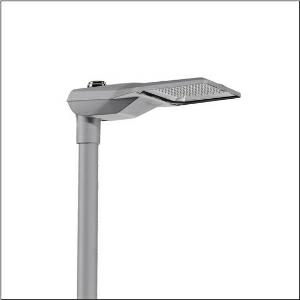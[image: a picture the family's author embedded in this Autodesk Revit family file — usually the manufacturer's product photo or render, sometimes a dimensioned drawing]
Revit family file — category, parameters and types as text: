
# Revit family: streetlight_sl_21_midi___st1_0a_5xe7d27n08nb_1197
name_source: partatom
category: Lighting Fixtures
units: mm (PartAtom-declared; Revit-internal decimal feet)

## family parameters
Cut with Voids When Loaded = No
Host = Face
Light Source = No
Part Type = Normal
Room Calculation Point = No
Round Connector Dimension = Use Diameter
Shared = No

## types (1)
- --- (1 x LED, 18780 lm, 151.2 W, 2200K)
    Apparent Load = 151 VA
    CIE Flux Codes = 40 73 97 100 100
    Color Rendering = 70
    Color Temperature = 2200K
    Default Elevation = 1800 mm
    Description = Streetlight SL 21 midi, mast luminaire, primary light control with lens, of PMMA, primary optical cover: cover, of toughened safety glass, transparent, light distribution: ST1.0a, light emission: direct distribution, primary light characteristic: asymmetric, installation type: side-entry, LED, 3G 2.5mm², High Power LED, rated luminous flux: 18.780lm, luminous efficacy: 124lm/W, light colour: 722, colour temperature: 2200K, control gear: NEMA (7pin), control: overheat protection, pre-setting: linear dimming characteristic, constant luminous flux control, time-dependent luminous flux control, flexible luminous flux parameterisation, mains connection: 220..240V, AC, 50/60Hz, connection cable pre-assembled, cable length: 12,5m, wiring characteristics: H05VV-F, start of lifetime: 151W, end of service life: 157W, reduction: 70W, luminaire housing, of diecast aluminium (EN AC-44300), powder-coated, SITECO metallic grey (DB 702S), corrosivity category C5 high according to DIN EN ISO 12944, multi-level sealing system, sealing non-destructively replaceable, inclination adjustable: 0°, 5°, 10°, 15°, length: 644mm, width: 335mm, height: 110mm, spigot size: 42mm (side-entry), mounting height: 4..8m, protection rating (complete): IP66, insulation class (complete): insulation class I (protective earthing), certification: CE, ENEC, ENEC+, VDE, impact resistance: IK10, permissible operating ambient temperature for outdoor applications: -40..+50°C, standard-compliant lighting for roads and squares, packaging unit: 1 piece

Light Distribution: ST1.0a
    Height = 111 mm
    Lamp = 1 x LED
    Lamp Light Flux = 18780 lm
    Lamp Power = 151.2 W
    Lamp count = 1
    Length = 644 mm
    Luminous efficacy = 124 lm/W
    Manufacturer = Siteco
    ModVariant = No
    Model = 5XE7D27N08NB
    Number of Poles = 1
    OnlyDefault = Yes
    Power Factor = 1
    Product Name = Streetlight SL 21 midi | ST1.0a
    Product group = mast luminaire | pylon top
    ProductGroupID = 6100
    Protection Class = Protection class I
    Protection Degree = IP 66
    RLX_Detail_Level = 1
    RLX_Emergency_Light_Flux = 0 lm
    RLX_Emergency_Type = 0
    RLX_Emergency_Type_DB = No
    RlxData = <blob elided: 26613 chars, md5=731fe4ec>
    Socket = socket
    Standby Power = 0 W
    System Light Flux = 18781 lm
    System Power = 151 W
    Type Comments = factory setting: luminous flux: 100 % | dim-lin: 254 | 802 mA
    Type Image = l_1294377.jpg
    URL = http://relux.com
    VarID = @adj_134699
    Voltage = 0 V
    Weight = 0.00 kg
    Width = 336 mm

## geometry (parser evidence)
native form markers: Blend x4, Sweep x9
no freeform markers — native parametric forms only
